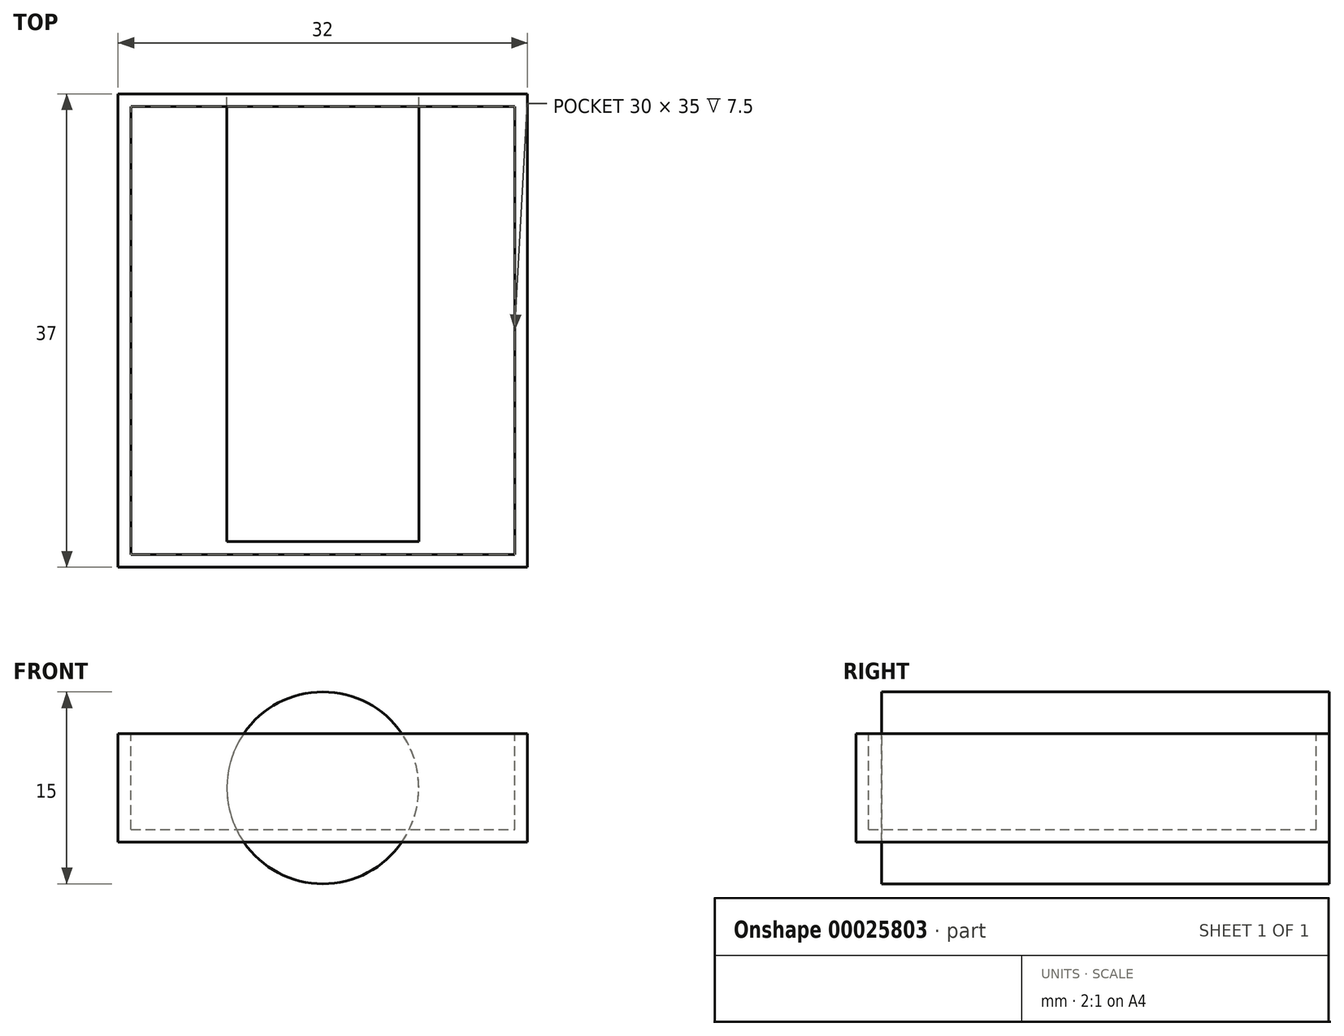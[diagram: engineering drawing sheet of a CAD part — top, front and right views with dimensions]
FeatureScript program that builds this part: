
annotation { "Feature Type Name" : "Feature", "Feature Type Description" : "" }
export const myFeature = defineFeature(function(context is Context, id is Id, definition is map)
    precondition{}
    {
        {
            var Q0;
            Q0=qCreatedBy(makeId("Front.planeOp"),FACE);
            var sketch = newSketch(context, id + "F0", { "sketchPlane" : qUnion([Q0])});
            skLineSegment(sketch, "E0.rect.bottom", {"start": v(-16, -4.25) * mm, "end": v(16, -4.25) * mm});
            skLineSegment(sketch, "E0.rect.top", {"start": v(-16, 4.25) * mm, "end": v(16, 4.25) * mm});
            skLineSegment(sketch, "E0.rect.left", {"start": v(-16, -4.25) * mm, "end": v(-16, 4.25) * mm});
            skLineSegment(sketch, "E0.rect.right", {"start": v(16, -4.25) * mm, "end": v(16, 4.25) * mm});
            skPoint(sketch, "E0.rect.middle", {"position": v(0, 0) * mm});
            skSolve(sketch);
        }
        {
            var Q0;
            Q0=makeQuery(id+"F0.imprint","IMPRINT",FACE,{"disambiguationData":[TD([[makeQuery(id+"F0.imprint","IMPRINT",EDGE,{"derivedFrom":sQuery(id+"F0.wireOp",EDGE,"E0.rect.bottom")}),1.0]])]});
            extrude(context, id + "F1", {"entities" : qUnion([Q0]), "depth" : 37 * mm});
        }
        {
            var Q0;
            Q0=qCreatedBy(makeId("Front.planeOp"),FACE);
            var sketch = newSketch(context, id + "F2", { "sketchPlane" : qUnion([Q0])});
            skCircle(sketch, "E1", {"center": v(0, 0) * mm, "radius": 7.5 * mm});
            skSolve(sketch);
        }
        {
            var Q0;
            Q0=makeQuery(id+"F2.imprint","IMPRINT",FACE,{"disambiguationData":[TD([[makeQuery(id+"F2.imprint","IMPRINT",EDGE,{"derivedFrom":sQuery(id+"F2.wireOp",EDGE,"E1")}),1.0]])]});
            extrude(context, id + "F3", {"entities" : qUnion([Q0]), "depth" : 35 * mm});
        }
        {
            var Q0;
            Q0=makeQuery(id+"F1.opExtrude","SWEPT_FACE",FACE,{"disambiguationData":[OSD([sQuery(id+"F0.wireOp",EDGE,"E0.rect.top")])]});
            shell(context, id + "F4", {"entities" : qUnion([Q0]), "thickness" : 1 * mm});
        }
    });
